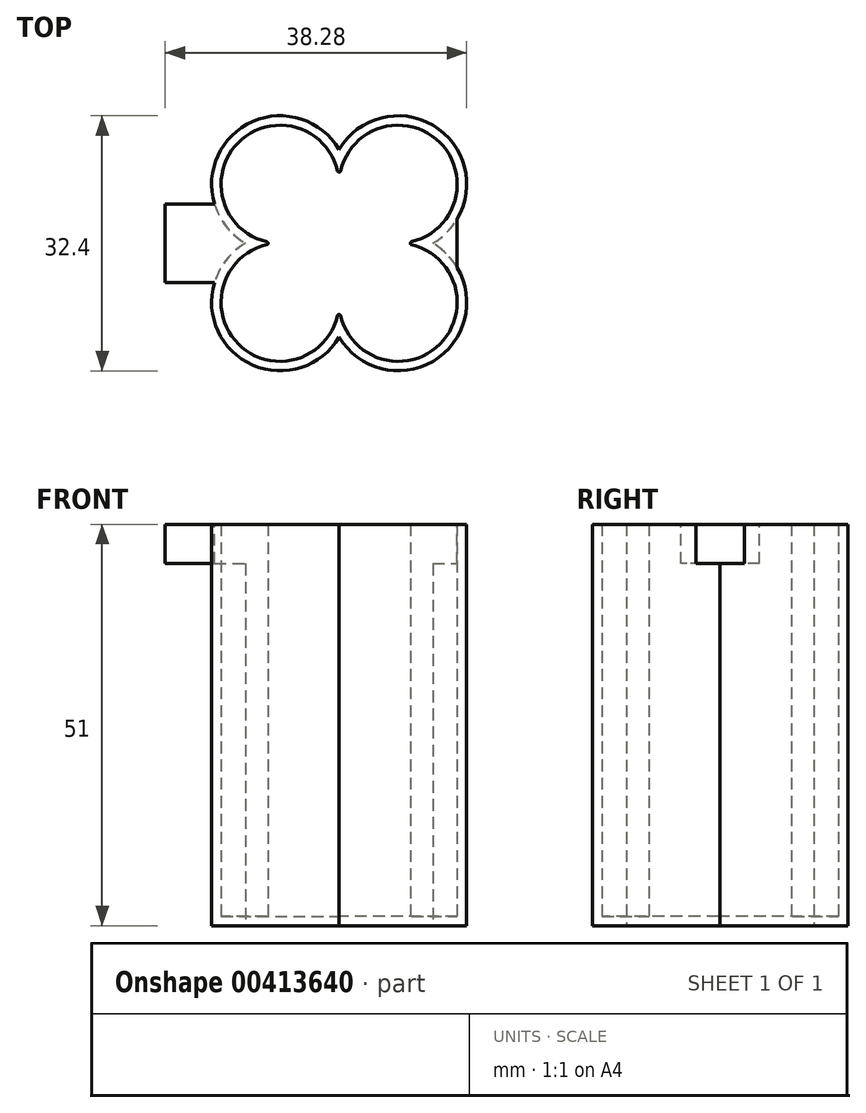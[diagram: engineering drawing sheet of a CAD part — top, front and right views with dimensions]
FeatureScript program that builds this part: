
annotation { "Feature Type Name" : "Feature", "Feature Type Description" : "" }
export const myFeature = defineFeature(function(context is Context, id is Id, definition is map)
    precondition{}
    {
        {
            var Q0;
            Q0=qCreatedBy(makeId("Top.planeOp"),FACE);
            var sketch = newSketch(context, id + "F0", { "sketchPlane" : qUnion([Q0])});
            skCircle(sketch, "E0", {"center": v(0, 0) * mm, "radius": 12.5 * mm});
            skLineSegment(sketch, "E1", {"start": v(-10, 7.5) * mm, "end": v(-10, -7.5) * mm});
            skLineSegment(sketch, "E2", {"start": v(10, 7.5) * mm, "end": v(10, -7.5) * mm});
            skSolve(sketch);
        }
        {
            var Q0;
            Q0=qCreatedBy(makeId("Top.planeOp"),FACE);
            var sketch = newSketch(context, id + "F1", { "sketchPlane" : qUnion([Q0])});
            skArc(sketch, "E3", {"start": v(9.2, 0.2) * mm, "mid": v(12.8, 12.8) * mm, "end": v(0.2, 9.2) * mm});
            skArc(sketch, "E4", {"start": v(0.2, -9.2) * mm, "mid": v(12.8, -12.8) * mm, "end": v(9.2, -0.2) * mm});
            skArc(sketch, "E5", {"start": v(-9.2, -0.2) * mm, "mid": v(-12.8, -12.8) * mm, "end": v(-0.2, -9.2) * mm});
            skArc(sketch, "E6", {"start": v(-0.2, 9.2) * mm, "mid": v(-12.8, 12.8) * mm, "end": v(-9.2, 0.2) * mm});
            skArc(sketch, "E7.0", {"start": v(0, 11.9) * mm, "mid": v(-13.65, 13.65) * mm, "end": v(-11.9, 0) * mm});
            skArc(sketch, "E8.0", {"start": v(-11.9, 0) * mm, "mid": v(-13.65, -13.65) * mm, "end": v(0, -11.9) * mm});
            skArc(sketch, "E9.trimOffspring", {"start": v(11.9, 0) * mm, "mid": v(13.65, 13.65) * mm, "end": v(0, 11.9) * mm});
            skArc(sketch, "E10.trimOffspring", {"start": v(0, -11.9) * mm, "mid": v(13.65, -13.65) * mm, "end": v(11.9, 0) * mm});
            skPoint(sketch, "E11.visualSharp", {"position": v(0, 7.5) * mm});
            skArc(sketch, "E11.filletArc", {"start": v(-0.2, 9.2) * mm, "mid": v(0, 9.04) * mm, "end": v(0.2, 9.2) * mm});
            skPoint(sketch, "E12.visualSharp", {"position": v(-7.5, 0) * mm});
            skArc(sketch, "E12.filletArc", {"start": v(-9.2, -0.2) * mm, "mid": v(-9.04, 0) * mm, "end": v(-9.2, 0.2) * mm});
            skPoint(sketch, "E13.visualSharp", {"position": v(0, -7.5) * mm});
            skArc(sketch, "E13.filletArc", {"start": v(0.2, -9.2) * mm, "mid": v(0, -9.04) * mm, "end": v(-0.2, -9.2) * mm});
            skPoint(sketch, "E14.visualSharp", {"position": v(7.5, 0) * mm});
            skArc(sketch, "E14.filletArc", {"start": v(9.2, 0.2) * mm, "mid": v(9.04, 0) * mm, "end": v(9.2, -0.2) * mm});
            skSolve(sketch);
        }
        {
            var Q0;
            Q0=makeQuery(id+"F1.imprint","IMPRINT",FACE,{"disambiguationData":[TD([[makeQuery(id+"F1.imprint","IMPRINT",EDGE,{"derivedFrom":sQuery(id+"F1.wireOp",EDGE,"E3")}),-1.0]])]});
            extrude(context, id + "F2", {"entities" : qUnion([Q0]), "depth" : 51 * mm});
        }
        {
            var Q0;
            Q0=makeQuery(id+"F1.imprint","IMPRINT",FACE,{"disambiguationData":[TD([[makeQuery(id+"F1.imprint","IMPRINT",EDGE,{"derivedFrom":sQuery(id+"F1.wireOp",EDGE,"E3")}),1.0]])]});
            extrude(context, id + "F3", {"entities" : qUnion([Q0]), "operationType" : NewBodyOperationType.ADD, "depth" : 1.2 * mm});
        }
        {
            var Q0;
            Q0=makeQuery(id+"F2.opExtrude","CAP_FACE",FACE,{"disambiguationData":[OSD([sQuery(id+"F1.wireOp",EDGE,"E3"),sQuery(id+"F1.wireOp",EDGE,"E4"),sQuery(id+"F1.wireOp",EDGE,"E5"),sQuery(id+"F1.wireOp",EDGE,"E6"),sQuery(id+"F1.wireOp",EDGE,"E7.0"),sQuery(id+"F1.wireOp",EDGE,"E8.0"),sQuery(id+"F1.wireOp",EDGE,"E9.trimOffspring"),sQuery(id+"F1.wireOp",EDGE,"E10.trimOffspring"),sQuery(id+"F1.wireOp",EDGE,"E11.filletArc"),sQuery(id+"F1.wireOp",EDGE,"E12.filletArc"),sQuery(id+"F1.wireOp",EDGE,"E13.filletArc"),sQuery(id+"F1.wireOp",EDGE,"E14.filletArc")])],"isStart":false});
            var sketch = newSketch(context, id + "F4", { "sketchPlane" : qUnion([Q0])});
            skLineSegment(sketch, "E15", {"start": v(-15.08, 5) * mm, "end": v(-22.08, 5) * mm});
            skLineSegment(sketch, "E16", {"start": v(-22.08, 5) * mm, "end": v(-22.08, -5) * mm});
            skLineSegment(sketch, "E17", {"start": v(-22.08, -5) * mm, "end": v(-15.08, -5) * mm});
            skPoint(sketch, "E18.end.orphan", {"position": v(-10.1, 0) * mm});
            skLineSegment(sketch, "E19", {"start": v(-15.08, 5) * mm, "end": v(-14.02, 2.3) * mm});
            skLineSegment(sketch, "E20", {"start": v(-14.02, 2.3) * mm, "end": v(-10.1, 0) * mm});
            skLineSegment(sketch, "E21", {"start": v(-10.1, 0) * mm, "end": v(-13.9, -2.43) * mm});
            skLineSegment(sketch, "E22", {"start": v(-13.9, -2.43) * mm, "end": v(-15.08, -5) * mm});
            skLineSegment(sketch, "E23", {"start": v(15, 4.2) * mm, "end": v(15, -4.34) * mm});
            skLineSegment(sketch, "E24", {"start": v(15, 4.2) * mm, "end": v(11.2, 0) * mm});
            skLineSegment(sketch, "E25", {"start": v(11.2, 0) * mm, "end": v(15, -4.34) * mm});
            skSolve(sketch);
        }
        {
            var Q0;
            {var subQ6=sQuery(id+"F4.wireOp",EDGE,"E16");Q0=makeQuery(id+"F4.imprint","IMPRINT",FACE,{"disambiguationData":[TD([[makeQuery(id+"F4.imprint","IMPRINT",EDGE,{"derivedFrom":subQ6}),1.0]])]});}
            extrude(context, id + "F5", {"entities" : qUnion([Q0]), "operationType" : NewBodyOperationType.ADD, "oppositeDirection" : true, "depth" : 5 * mm});
        }
        {
            var Q0;
            {var subQ0=sQuery(id+"F4.wireOp",EDGE,"E23");var subQ1=makeQuery(id+"F2.opExtrude","CAP_EDGE",EDGE,{"disambiguationData":[OSD([sQuery(id+"F1.wireOp",EDGE,"E9.trimOffspring")])],"isStart":false});var subQ2=makeQuery(id+"F4.imprint","INTERSECT",VERTEX,{"derivedFrom":[subQ1,subQ0]});Q0=makeQuery(id+"F4.imprint","IMPRINT",FACE,{"disambiguationData":[TD([[makeQuery(id+"F4.imprint","IMPRINT",EDGE,{"disambiguationData":[TD([[subQ2,-1.0]])],"derivedFrom":subQ0}),-1.0]])]});}
            extrude(context, id + "F6", {"entities" : qUnion([Q0]), "operationType" : NewBodyOperationType.ADD, "oppositeDirection" : true, "depth" : 5 * mm});
        }
    });
